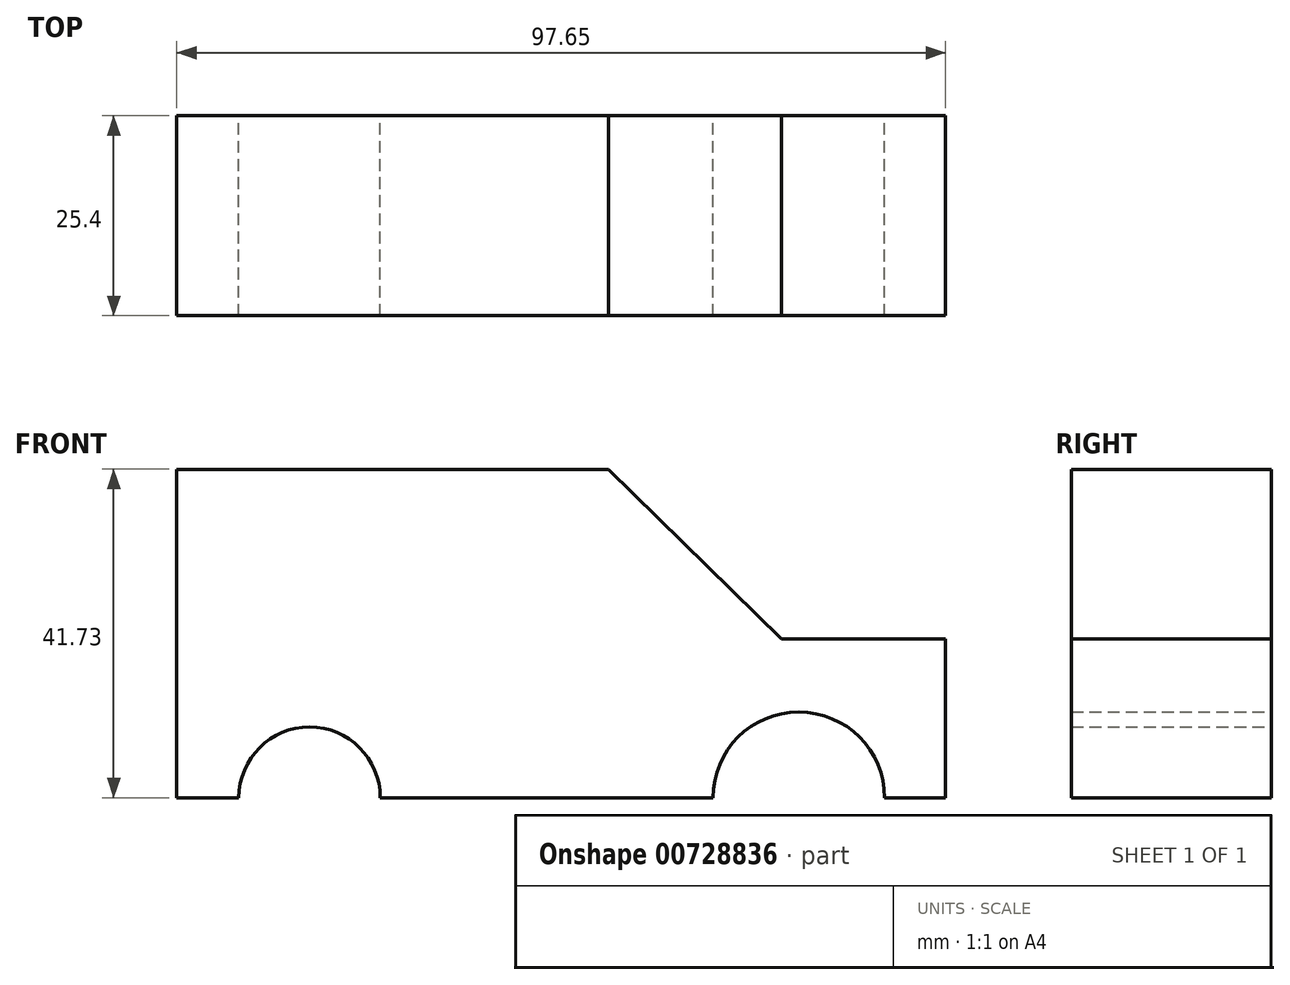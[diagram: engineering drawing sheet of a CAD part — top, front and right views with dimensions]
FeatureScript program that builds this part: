
annotation { "Feature Type Name" : "Feature", "Feature Type Description" : "" }
export const myFeature = defineFeature(function(context is Context, id is Id, definition is map)
    precondition{}
    {
        {
            var Q0;
            Q0=qCreatedBy(makeId("Front.planeOp"),FACE);
            var sketch = newSketch(context, id + "F0", { "sketchPlane" : qUnion([Q0])});
            skLineSegment(sketch, "E0", {"start": v(0, 0) * mm, "end": v(13.3, 0) * mm});
            skLineSegment(sketch, "E1", {"start": v(42.83, 0) * mm, "end": v(42.83, 20.2) * mm});
            skLineSegment(sketch, "E2", {"start": v(42.83, 20.2) * mm, "end": v(21.97, 20.2) * mm});
            skLineSegment(sketch, "E3", {"start": v(21.97, 20.2) * mm, "end": v(0, 41.73) * mm});
            skLineSegment(sketch, "E4", {"start": v(0, 41.73) * mm, "end": v(-54.82, 41.73) * mm});
            skLineSegment(sketch, "E5", {"start": v(-54.82, 41.73) * mm, "end": v(-54.82, 0) * mm});
            skLineSegment(sketch, "E6", {"start": v(-54.82, 0) * mm, "end": v(-46.94, 0) * mm});
            skArc(sketch, "E7", {"start": v(-28.96, 0) * mm, "mid": v(-37.95, 8.99) * mm, "end": v(-46.94, 0) * mm});
            skArc(sketch, "E8", {"start": v(35.09, 0) * mm, "mid": v(24.2, 10.9) * mm, "end": v(13.3, 0) * mm});
            skLineSegment(sketch, "E9.trimOffspring", {"start": v(-28.96, 0) * mm, "end": v(0, 0) * mm});
            skLineSegment(sketch, "E10.trimOffspring", {"start": v(35.09, 0) * mm, "end": v(42.83, 0) * mm});
            skSolve(sketch);
        }
        {
            var Q0;
            Q0 = qSketchRegion(id + "F0", true);
            extrude(context, id + "F1", {"entities" : qUnion([Q0]), "depth" : 25.4 * mm, "offsetDistance" : 25.4 * mm});
        }
    });
